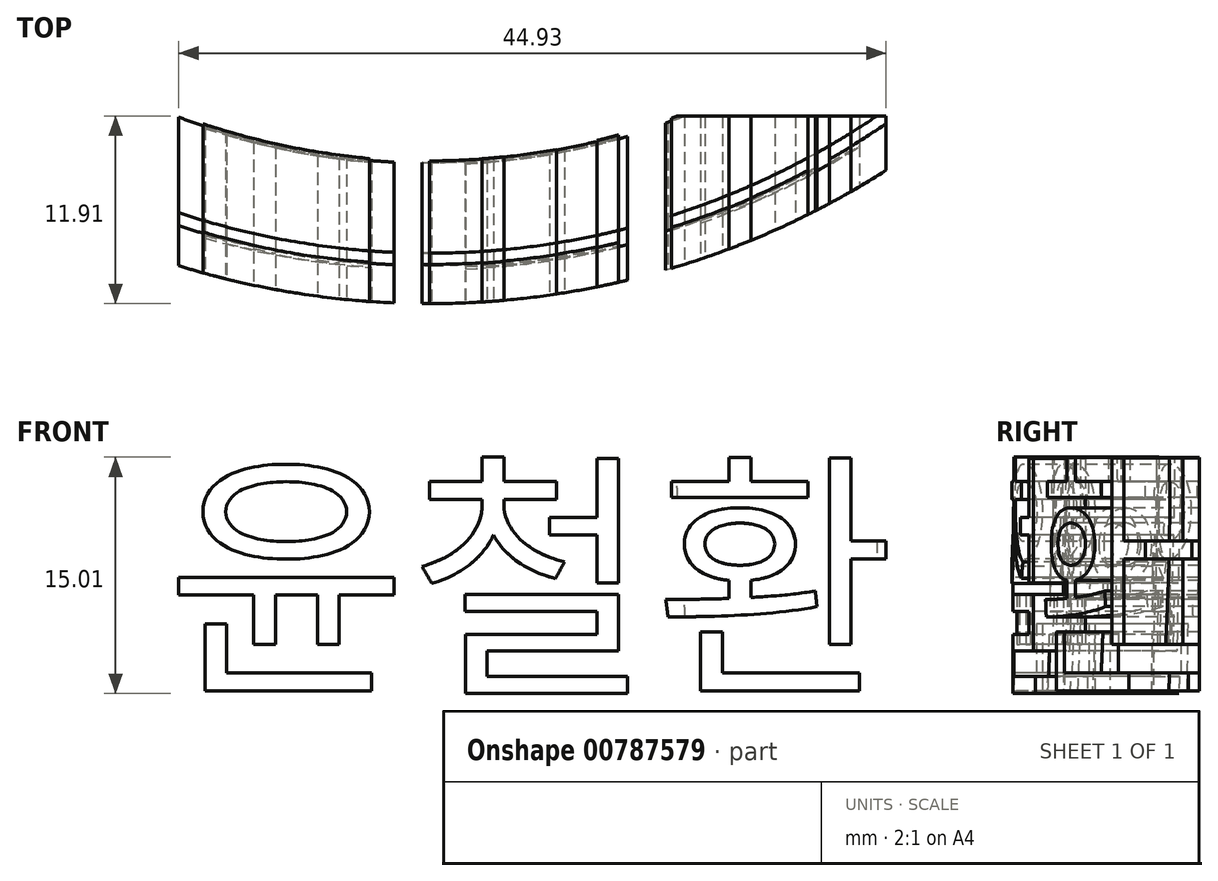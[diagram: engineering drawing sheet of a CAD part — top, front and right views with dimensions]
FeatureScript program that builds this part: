
annotation { "Feature Type Name" : "Feature", "Feature Type Description" : "" }
export const myFeature = defineFeature(function(context is Context, id is Id, definition is map)
    precondition{}
    {
        {
            var Q0;
            Q0=qCreatedBy(makeId("Front.planeOp"),FACE);
            var sketch = newSketch(context, id + "F0", { "sketchPlane" : qUnion([Q0])});
            skFitSpline(sketch, "E0", {"points": [v(-5.84, -23.92) * mm, v(-22.55, -24.15) * mm, v(-31.48, -24.15) * mm, v(-41.32, -23.92) * mm, v(-45.21, -20.26) * mm, v(-45.44, -12.25) * mm, v(-45.44, -2.17) * mm, v(-45.21, 12.02) * mm, v(-44.98, 33.77) * mm, v(-45.44, 48.42) * mm, v(-47.96, 53) * mm, v(-51.62, 55.97) * mm, v(-54.37, 54.14) * mm, v(-52.54, 49.8) * mm, v(-51.85, 23.7) * mm, v(-51.85, 11.56) * mm, v(-52.3, 2.17) * mm, v(-52.3, 0) * mm, v(-52.54, -8.58) * mm, v(-53, -20.49) * mm, v(-52.3, -25.75) * mm, v(-49.8, -30.33) * mm, v(-42.7, -31.02) * mm, v(-34.68, -31.25) * mm, v(-24.84, -31.25) * mm, v(-16.37, -31.25) * mm, v(-2.4, -31.02) * mm], "startDerivative": vector(-402.4, 9.15) * mm, "endDerivative": vector(290.92, 0) * mm});
            skFitSpline(sketch, "E1", {"points": [v(-5.84, -23.92) * mm, v(0, -23.92) * mm], "startDerivative": vector(5.84, 0) * mm, "endDerivative": vector(5.84, 0) * mm});
            skFitSpline(sketch, "E2", {"points": [v(-2.4, -31.02) * mm, v(0, -31.02) * mm], "startDerivative": vector(2.4, 0) * mm, "endDerivative": vector(2.4, 0) * mm});
            skLineSegment(sketch, "E3", {"start": v(0, 63.07) * mm, "end": v(0, -54.83) * mm});
            skSolve(sketch);
        }
        {
            var Q0;
            Q0=makeQuery(id+"F0.imprint","IMPRINT",FACE,{"disambiguationData":[TD([[makeQuery(id+"F0.imprint","IMPRINT",EDGE,{"derivedFrom":sQuery(id+"F0.wireOp",EDGE,"E0")}),1.0]])]});
            var Q1;
            Q1=sQuery(id+"F0.wireOp",EDGE,"E3");
            revolve(context, id + "F1", {"surfaceOperationType" : NewSurfaceOperationType.NEW, "entities" : qUnion([Q0]), "axis" : qUnion([Q1]), "revolveType" : RevolveType.FULL});
        }
        {
            var Q0;
            Q0=qCreatedBy(makeId("Front.planeOp"),FACE);
            var sketch = newSketch(context, id + "F2", { "sketchPlane" : qUnion([Q0])});
            skFitSpline(sketch, "E4", {"points": [v(51.4, 38.57) * mm, v(67.19, 57.35) * mm, v(89.62, 31.25) * mm, v(85.27, -0.8) * mm, v(70.62, -17.05) * mm, v(56.43, -20.03) * mm, v(50.02, -20.49) * mm], "startDerivative": vector(76.06, 157.41) * mm, "endDerivative": vector(-62.04, -4.6) * mm});
            skSolve(sketch);
        }
        {
            var Q0;
            Q0=qCreatedBy(makeId("Right.planeOp"),FACE);
            var Q1;
            Q1 = qBodyType(qCreatedBy(id + "F4" ,EDGE), BodyType.WIRE);
            cPlane(context, id + "F3", {"entities" : qUnion([Q0, Q1]), "cplaneType" : CPlaneType.OFFSET, "offset" : 50 * mm, "width" : 150 * mm, "height" : 150 * mm});
        }
        {
            var Q0;
            Q0=qCreatedBy(id+"F3.planeOp",FACE);
            var sketch = newSketch(context, id + "F4", { "sketchPlane" : qUnion([Q0])});
            skCircle(sketch, "E5", {"center": v(0, 38.57) * mm, "radius": 4.67 * mm});
            skSolve(sketch);
        }
        {
            var Q0;
            Q0 = qSketchRegion(id + "F4", true);
            var Q1;
            Q1=sQuery(id+"F2.wireOp",EDGE,"E4");
            sweep(context, id + "F5", {"profiles" : qUnion([Q0]), "path" : qUnion([Q1])});
        }
        {
            var Q0;
            Q0=qCreatedBy(makeId("Front.planeOp"),FACE);
            cPlane(context, id + "F6", {"entities" : qUnion([Q0]), "cplaneType" : CPlaneType.OFFSET, "offset" : 60 * mm, "width" : 150 * mm, "height" : 150 * mm});
        }
        {
            var Q0;
            Q0=qCreatedBy(id+"F6.planeOp",FACE);
            var sketch = newSketch(context, id + "F7", { "sketchPlane" : qUnion([Q0])});
            skText(sketch, "E6", { "text": "윤철환", "fontName": "NotoSansCJKkr-Regular.otf"});
            const initialGuessF7  = {"E6": [-0.01682, 0.02759, 1, 0, 0.01213]};
            skSetInitialGuess(sketch, initialGuessF7);
            skSolve(sketch);
        }
        {
            var Q0;
            Q0=qCreatedBy(makeId("Front.planeOp"),FACE);
            var sketch = newSketch(context, id + "F8", { "sketchPlane" : qUnion([Q0])});
            skLineSegment(sketch, "E7.bottom", {"start": v(-53.9, 42.92) * mm, "end": v(-50.7, 42.92) * mm});
            skLineSegment(sketch, "E7.top", {"start": v(-53.9, 16.83) * mm, "end": v(-50.7, 16.83) * mm});
            skLineSegment(sketch, "E7.left", {"start": v(-53.9, 42.92) * mm, "end": v(-53.9, 16.83) * mm});
            skLineSegment(sketch, "E7.right", {"start": v(-50.7, 42.92) * mm, "end": v(-50.7, 16.83) * mm});
            skSolve(sketch);
        }
        {
            var Q0;
            Q0=makeQuery(id+"F8.imprint","IMPRINT",FACE,{"disambiguationData":[TD([[makeQuery(id+"F8.imprint","IMPRINT",EDGE,{"derivedFrom":sQuery(id+"F8.wireOp",EDGE,"E7.bottom")}),-1.0]])]});
            var Q1;
            Q1=sQuery(id+"F0.wireOp",EDGE,"E3");
            revolve(context, id + "F9", {"surfaceOperationType" : NewSurfaceOperationType.NEW, "entities" : qUnion([Q0]), "axis" : qUnion([Q1]), "revolveType" : RevolveType.ONE_DIRECTION, "oppositeDirection" : true, "angle" : 150 * degree});
        }
        {
            var Q0;
            Q0 = qSketchRegion(id + "F7", true);
            extrude(context, id + "F10", {"entities" : qUnion([Q0]), "operationType" : NewBodyOperationType.INTERSECT, "oppositeDirection" : true, "depth" : 18 * mm, "offsetDistance" : 25 * mm});
        }
    });
